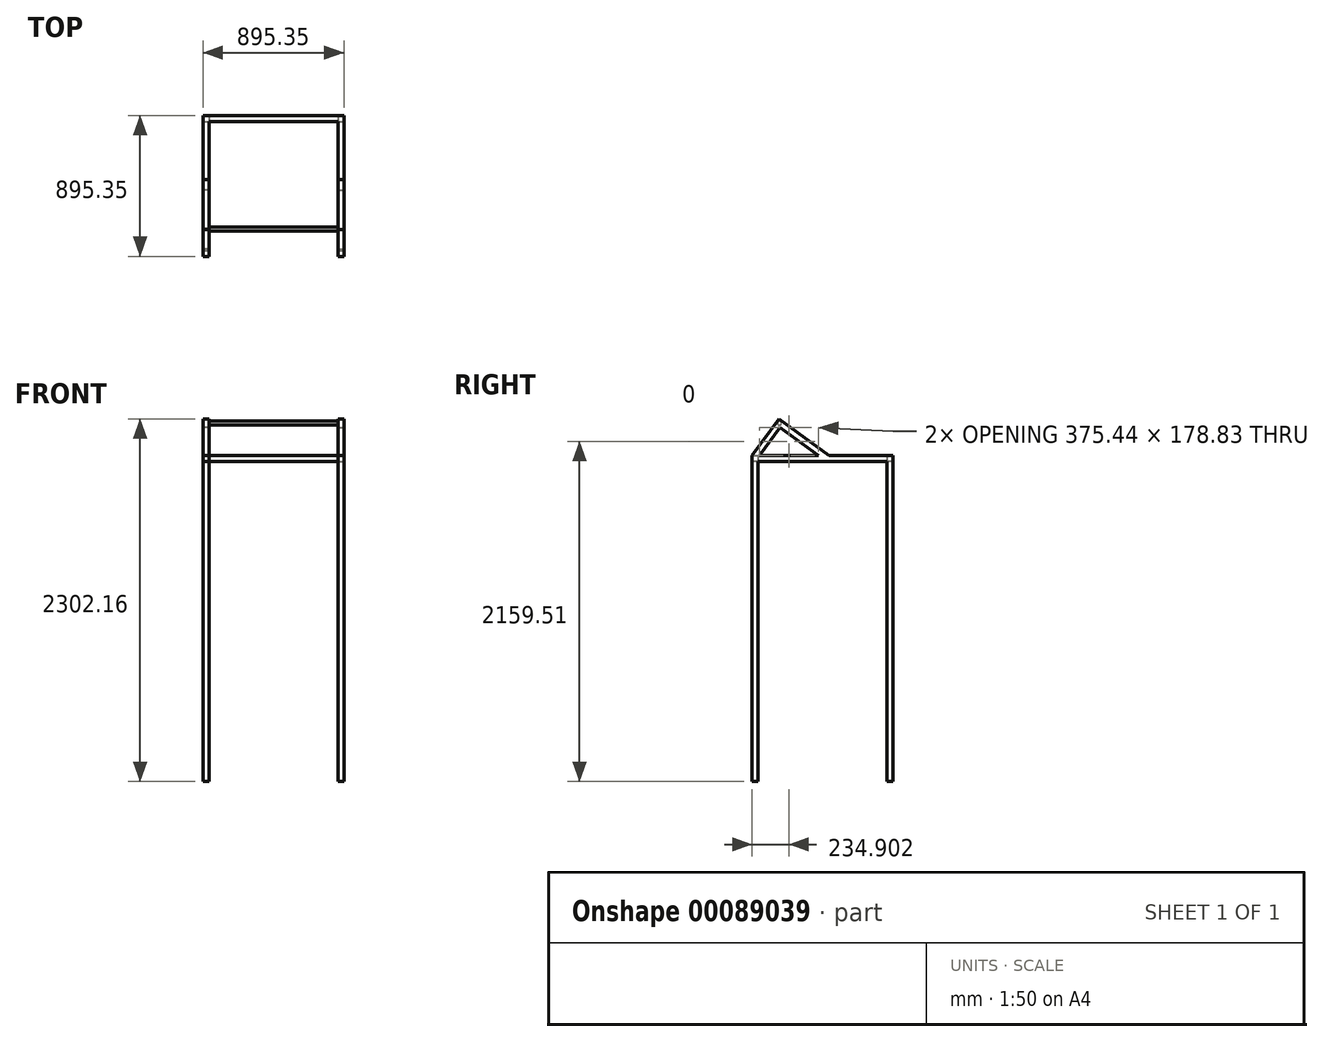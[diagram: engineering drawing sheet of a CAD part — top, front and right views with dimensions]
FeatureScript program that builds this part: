
annotation { "Feature Type Name" : "Feature", "Feature Type Description" : "" }
export const myFeature = defineFeature(function(context is Context, id is Id, definition is map)
    precondition{}
    {
        {
            var Q0;
            Q0=qCreatedBy(makeId("Top.planeOp"),FACE);
            var sketch = newSketch(context, id + "F0", { "sketchPlane" : qUnion([Q0])});
            skLineSegment(sketch, "E0.bottom", {"start": v(0, 0) * mm, "end": v(857.25, 0) * mm, "construction": true});
            skLineSegment(sketch, "E0.top", {"start": v(0, 857.25) * mm, "end": v(857.25, 857.25) * mm, "construction": true});
            skLineSegment(sketch, "E0.left", {"start": v(0, 0) * mm, "end": v(0, 857.25) * mm, "construction": true});
            skLineSegment(sketch, "E0.right", {"start": v(857.25, 0) * mm, "end": v(857.25, 857.25) * mm, "construction": true});
            skLineSegment(sketch, "E1.bottom", {"start": v(-19.05, 876.3) * mm, "end": v(19.05, 876.3) * mm});
            skLineSegment(sketch, "E1.top", {"start": v(-19.05, 838.2) * mm, "end": v(19.05, 838.2) * mm});
            skLineSegment(sketch, "E1.left", {"start": v(-19.05, 876.3) * mm, "end": v(-19.05, 838.2) * mm});
            skLineSegment(sketch, "E1.right", {"start": v(19.05, 876.3) * mm, "end": v(19.05, 838.2) * mm});
            skLineSegment(sketch, "E2", {"start": v(-19.05, 876.3) * mm, "end": v(19.05, 838.2) * mm, "construction": true});
            skLineSegment(sketch, "E3.bottom", {"start": v(838.2, 876.3) * mm, "end": v(876.3, 876.3) * mm});
            skLineSegment(sketch, "E3.top", {"start": v(838.2, 838.2) * mm, "end": v(876.3, 838.2) * mm});
            skLineSegment(sketch, "E3.left", {"start": v(838.2, 876.3) * mm, "end": v(838.2, 838.2) * mm});
            skLineSegment(sketch, "E3.right", {"start": v(876.3, 876.3) * mm, "end": v(876.3, 838.2) * mm});
            skLineSegment(sketch, "E4.bottom", {"start": v(-19.05, 19.05) * mm, "end": v(19.05, 19.05) * mm});
            skLineSegment(sketch, "E4.top", {"start": v(-19.05, -19.05) * mm, "end": v(19.05, -19.05) * mm});
            skLineSegment(sketch, "E4.left", {"start": v(-19.05, 19.05) * mm, "end": v(-19.05, -19.05) * mm});
            skLineSegment(sketch, "E4.right", {"start": v(19.05, 19.05) * mm, "end": v(19.05, -19.05) * mm});
            skLineSegment(sketch, "E5.bottom", {"start": v(838.2, 19.05) * mm, "end": v(876.3, 19.05) * mm});
            skLineSegment(sketch, "E5.top", {"start": v(838.2, -19.05) * mm, "end": v(876.3, -19.05) * mm});
            skLineSegment(sketch, "E5.left", {"start": v(838.2, 19.05) * mm, "end": v(838.2, -19.05) * mm});
            skLineSegment(sketch, "E5.right", {"start": v(876.3, 19.05) * mm, "end": v(876.3, -19.05) * mm});
            skLineSegment(sketch, "E6", {"start": v(838.2, 19.05) * mm, "end": v(876.3, -19.05) * mm, "construction": true});
            skSolve(sketch);
        }
        {
            var Q0;
            Q0 = qSketchRegion(id + "F0", true);
            extrude(context, id + "F1", {"entities" : qUnion([Q0]), "depth" : 2032 * mm});
        }
        {
            var Q0;
            Q0=makeQuery(id+"F1.opExtrude","CAP_FACE",FACE,{"disambiguationData":[OSD([sQuery(id+"F0.wireOp",EDGE,"E4.bottom"),sQuery(id+"F0.wireOp",EDGE,"E4.top"),sQuery(id+"F0.wireOp",EDGE,"E4.left"),sQuery(id+"F0.wireOp",EDGE,"E4.right")])],"isStart":false});
            var sketch = newSketch(context, id + "F2", { "sketchPlane" : qUnion([Q0])});
            skLineSegment(sketch, "E7", {"start": v(-19.05, -19.05) * mm, "end": v(-19.05, 876.3) * mm});
            skPoint(sketch, "E7.endSnap0", {"position": v(-19.05, 0) * mm});
            skLineSegment(sketch, "E8", {"start": v(-19.05, 876.3) * mm, "end": v(876.3, 876.3) * mm});
            skLineSegment(sketch, "E9", {"start": v(876.3, 876.3) * mm, "end": v(876.3, -19.05) * mm});
            skLineSegment(sketch, "E10", {"start": v(-19.05, -19.05) * mm, "end": v(19.05, -19.05) * mm});
            skLineSegment(sketch, "E11", {"start": v(19.05, -19.05) * mm, "end": v(19.05, 838.2) * mm});
            skLineSegment(sketch, "E12", {"start": v(19.05, 838.2) * mm, "end": v(838.2, 838.2) * mm});
            skLineSegment(sketch, "E13", {"start": v(838.2, 838.2) * mm, "end": v(838.2, -19.05) * mm});
            skLineSegment(sketch, "E14", {"start": v(838.2, -19.05) * mm, "end": v(876.3, -19.05) * mm});
            skLineSegment(sketch, "E15", {"start": v(19.05, -19.05) * mm, "end": v(-19.05, -19.05) * mm});
            skSolve(sketch);
        }
        {
            var Q0;
            {var subQ3=sQuery(id+"F2.wireOp",EDGE,"E8");Q0=makeQuery(id+"F2.imprint","IMPRINT",FACE,{"disambiguationData":[TD([[makeQuery(id+"F2.imprint","IMPRINT",EDGE,{"derivedFrom":subQ3}),-1.0]])]});}
            var Q1;
            {var subQ2=sQuery(id+"F2.wireOp",EDGE,"E15");Q1=makeQuery(id+"F2.imprint","IMPRINT",FACE,{"disambiguationData":[TD([[makeQuery(id+"F2.imprint","IMPRINT",EDGE,{"derivedFrom":subQ2}),1.0]])]});}
            extrude(context, id + "F3", {"entities" : qUnion([Q0, Q1]), "operationType" : NewBodyOperationType.ADD, "depth" : 38.1 * mm});
        }
        {
            var Q0;
            Q0=makeQuery(id+"F3.boolean.opBoolean","MERGE",FACE,{"derivedFrom":[makeQuery(id+"F1.opExtrude","SWEPT_FACE",FACE,{"disambiguationData":[OSD([sQuery(id+"F0.wireOp",EDGE,"E1.left")])]}),makeQuery(id+"F1.opExtrude","SWEPT_FACE",FACE,{"disambiguationData":[OSD([sQuery(id+"F0.wireOp",EDGE,"E4.left")])]}),makeQuery(id+"F3.opExtrude","SWEPT_FACE",FACE,{"disambiguationData":[OSD([sQuery(id+"F2.wireOp",EDGE,"E7")])]})]});
            var sketch = newSketch(context, id + "F4", { "sketchPlane" : qUnion([Q0])});
            skLineSegment(sketch, "E16", {"start": v(19.05, 2070.1) * mm, "end": v(-150.46, 2302.16) * mm});
            skLineSegment(sketch, "E17", {"start": v(-150.46, 2302.16) * mm, "end": v(-468.17, 2070.1) * mm});
            skLineSegment(sketch, "E18", {"start": v(-468.17, 2070.1) * mm, "end": v(-403.57, 2070.1) * mm});
            skLineSegment(sketch, "E19", {"start": v(-403.57, 2070.1) * mm, "end": v(-158.75, 2248.93) * mm});
            skLineSegment(sketch, "E20", {"start": v(-158.75, 2248.93) * mm, "end": v(-28.13, 2070.1) * mm});
            skLineSegment(sketch, "E21", {"start": v(-28.13, 2070.1) * mm, "end": v(19.05, 2070.1) * mm});
            skSolve(sketch);
        }
        {
            var Q0;
            Q0=makeQuery(id+"F4.imprint","IMPRINT",FACE,{"disambiguationData":[TD([[makeQuery(id+"F4.imprint","IMPRINT",EDGE,{"derivedFrom":sQuery(id+"F4.wireOp",EDGE,"E16")}),1.0]])]});
            extrude(context, id + "F5", {"entities" : qUnion([Q0]), "operationType" : NewBodyOperationType.ADD, "oppositeDirection" : true, "depth" : 38.1 * mm});
        }
        {
            var Q0;
            Q0=makeQuery(id+"F3.boolean.opBoolean","MERGE",FACE,{"derivedFrom":[makeQuery(id+"F1.opExtrude","SWEPT_FACE",FACE,{"disambiguationData":[OSD([sQuery(id+"F0.wireOp",EDGE,"E3.right")])]}),makeQuery(id+"F1.opExtrude","SWEPT_FACE",FACE,{"disambiguationData":[OSD([sQuery(id+"F0.wireOp",EDGE,"E5.right")])]}),makeQuery(id+"F3.opExtrude","SWEPT_FACE",FACE,{"disambiguationData":[OSD([sQuery(id+"F2.wireOp",EDGE,"E9")])]})]});
            var sketch = newSketch(context, id + "F6", { "sketchPlane" : qUnion([Q0])});
            skLineSegment(sketch, "E22.0", {"start": v(150.46, 2302.16) * mm, "end": v(468.17, 2070.1) * mm});
            skLineSegment(sketch, "E22.1", {"start": v(403.57, 2070.1) * mm, "end": v(158.75, 2248.93) * mm});
            skLineSegment(sketch, "E22.2", {"start": v(158.75, 2248.93) * mm, "end": v(28.13, 2070.1) * mm});
            skLineSegment(sketch, "E22.3", {"start": v(-19.05, 2070.1) * mm, "end": v(150.46, 2302.16) * mm});
            skLineSegment(sketch, "E23", {"start": v(468.17, 2070.1) * mm, "end": v(403.57, 2070.1) * mm});
            skLineSegment(sketch, "E24", {"start": v(28.13, 2070.1) * mm, "end": v(-19.05, 2070.1) * mm});
            skSolve(sketch);
        }
        {
            var Q0;
            Q0=makeQuery(id+"F6.imprint","IMPRINT",FACE,{"disambiguationData":[TD([[makeQuery(id+"F6.imprint","IMPRINT",EDGE,{"derivedFrom":sQuery(id+"F6.wireOp",EDGE,"E22.0")}),-1.0]])]});
            var Q1;
            Q1=makeQuery(id+"F3.boolean.opBoolean","MERGE",FACE,{"derivedFrom":[makeQuery(id+"F1.opExtrude","SWEPT_FACE",FACE,{"disambiguationData":[OSD([sQuery(id+"F0.wireOp",EDGE,"E5.left")])]}),makeQuery(id+"F3.opExtrude","SWEPT_FACE",FACE,{"disambiguationData":[OSD([sQuery(id+"F2.wireOp",EDGE,"E13")])]})]});
            extrude(context, id + "F7", {"entities" : qUnion([Q0]), "operationType" : NewBodyOperationType.ADD, "endBound" : BoundingType.UP_TO_SURFACE, "oppositeDirection" : true, "endBoundEntityFace" : qUnion([Q1]), "depth" : 25.4 * mm});
        }
        {
            var Q0;
            Q0=makeQuery(id+"F7.boolean.opBoolean","MERGE",FACE,{"derivedFrom":[makeQuery(id+"F3.boolean.opBoolean","MERGE",FACE,{"derivedFrom":[makeQuery(id+"F1.opExtrude","SWEPT_FACE",FACE,{"disambiguationData":[OSD([sQuery(id+"F0.wireOp",EDGE,"E5.left")])]}),makeQuery(id+"F3.opExtrude","SWEPT_FACE",FACE,{"disambiguationData":[OSD([sQuery(id+"F2.wireOp",EDGE,"E13")])]})]}),makeQuery(id+"F7.opExtrude","CAP_FACE",FACE,{"disambiguationData":[OSD([sQuery(id+"F6.wireOp",EDGE,"E22.0"),sQuery(id+"F6.wireOp",EDGE,"E22.1"),sQuery(id+"F6.wireOp",EDGE,"E22.2"),sQuery(id+"F6.wireOp",EDGE,"E22.3"),sQuery(id+"F6.wireOp",EDGE,"E23"),sQuery(id+"F6.wireOp",EDGE,"E24")])],"isStart":false})]});
            var sketch = newSketch(context, id + "F8", { "sketchPlane" : qUnion([Q0])});
            skCircle(sketch, "E25", {"center": v(-154.6, 2275.54) * mm, "radius": 12.7 * mm});
            skLineSegment(sketch, "E26", {"start": v(-150.46, 2302.16) * mm, "end": v(-158.75, 2248.93) * mm});
            skSolve(sketch);
        }
        {
            var Q0;
            {var subQ0=sQuery(id+"F8.wireOp",EDGE,"E26");var subQ1=sQuery(id+"F8.wireOp",EDGE,"E25");var subQ2=makeQuery(id+"F8.imprint","INTERSECT",VERTEX,{"disambiguationData":[OD(0.0)],"derivedFrom":[subQ1,subQ0]});Q0=makeQuery(id+"F8.imprint","IMPRINT",FACE,{"disambiguationData":[TD([[makeQuery(id+"F8.imprint","IMPRINT",EDGE,{"disambiguationData":[TD([[subQ2,-1.0]])],"derivedFrom":subQ1}),1.0]])]});}
            var Q1;
            {var subQ0=sQuery(id+"F8.wireOp",EDGE,"E26");var subQ1=sQuery(id+"F8.wireOp",EDGE,"E25");var subQ2=makeQuery(id+"F8.imprint","INTERSECT",VERTEX,{"disambiguationData":[OD(0.0)],"derivedFrom":[subQ1,subQ0]});Q1=makeQuery(id+"F8.imprint","IMPRINT",FACE,{"disambiguationData":[TD([[makeQuery(id+"F8.imprint","IMPRINT",EDGE,{"disambiguationData":[TD([[subQ2,1.0]])],"derivedFrom":subQ1}),1.0]])]});}
            extrude(context, id + "F9", {"entities" : qUnion([Q0, Q1]), "endBound" : BoundingType.UP_TO_NEXT, "depth" : 25.4 * mm});
        }
    });
